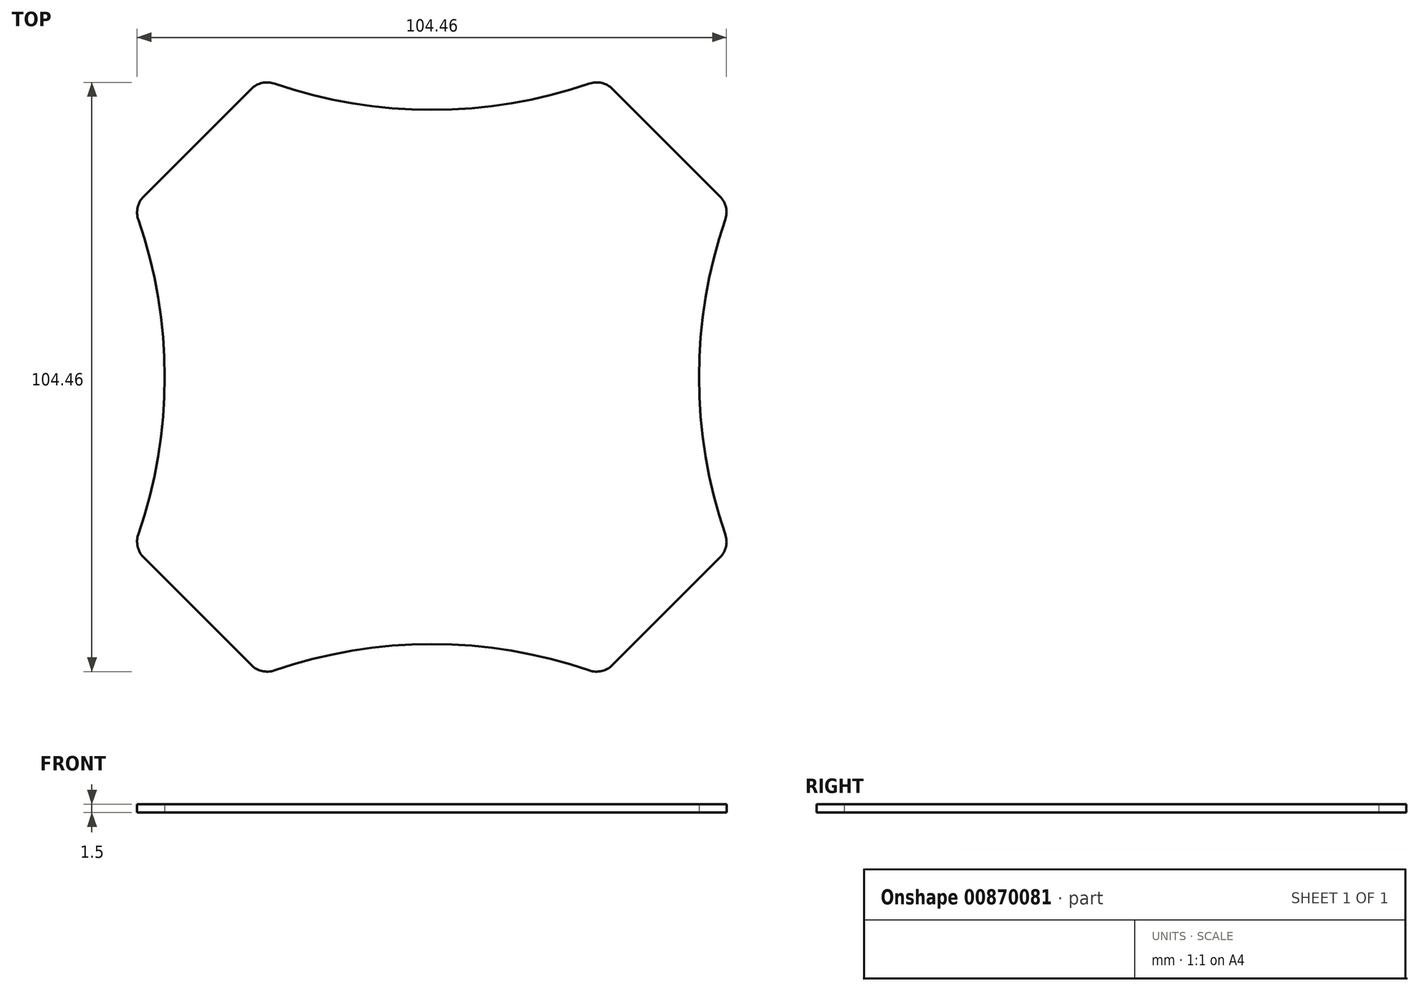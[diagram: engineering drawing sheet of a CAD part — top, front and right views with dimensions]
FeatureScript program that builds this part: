
annotation { "Feature Type Name" : "Feature", "Feature Type Description" : "" }
export const myFeature = defineFeature(function(context is Context, id is Id, definition is map)
    precondition{}
    {
        {
            var Q0;
            Q0=qCreatedBy(makeId("Top.planeOp"),FACE);
            var sketch = newSketch(context, id + "F0", { "sketchPlane" : qUnion([Q0])});
            skCircle(sketch, "E0.cCircle", {"center": v(0, 0) * mm, "radius": 58.75 * mm, "construction": true});
            skLineSegment(sketch, "E0.0", {"start": v(58.75, 24.34) * mm, "end": v(58.75, -24.34) * mm});
            skLineSegment(sketch, "E0.1", {"start": v(57.29, -25.8) * mm, "end": v(27.26, -55.82) * mm});
            skLineSegment(sketch, "E0.2", {"start": v(20.2, -58.75) * mm, "end": v(-20.2, -58.75) * mm});
            skLineSegment(sketch, "E0.3", {"start": v(-27.26, -55.82) * mm, "end": v(-57.29, -25.8) * mm});
            skLineSegment(sketch, "E0.4", {"start": v(-58.75, -24.34) * mm, "end": v(-58.75, 24.34) * mm});
            skLineSegment(sketch, "E0.5", {"start": v(-57.29, 25.8) * mm, "end": v(-27.26, 55.82) * mm});
            skLineSegment(sketch, "E0.6", {"start": v(-20.2, 58.75) * mm, "end": v(20.2, 58.75) * mm});
            skLineSegment(sketch, "E0.7", {"start": v(27.26, 55.82) * mm, "end": v(57.29, 25.8) * mm});
            skPoint(sketch, "E0.0.midPoint", {"position": v(58.75, 0) * mm});
            skLineSegment(sketch, "E1.bottom", {"start": v(60.82, 24.34) * mm, "end": v(85.75, 24.34) * mm});
            skLineSegment(sketch, "E1.top", {"start": v(60.82, -24.34) * mm, "end": v(85.75, -24.34) * mm});
            skLineSegment(sketch, "E1.right", {"start": v(90.75, 19.34) * mm, "end": v(90.75, -19.34) * mm});
            skLineSegment(sketch, "E2.bottom", {"start": v(-60.82, 24.34) * mm, "end": v(-85.75, 24.34) * mm});
            skLineSegment(sketch, "E2.top", {"start": v(-60.82, -24.34) * mm, "end": v(-85.75, -24.34) * mm});
            skLineSegment(sketch, "E2.left", {"start": v(-58.75, 24.34) * mm, "end": v(-58.75, -24.34) * mm});
            skLineSegment(sketch, "E2.right", {"start": v(-90.75, 19.34) * mm, "end": v(-90.75, -19.34) * mm});
            skPoint(sketch, "E3.visualSharp", {"position": v(-58.75, 24.34) * mm});
            skArc(sketch, "E3.filletArc", {"start": v(-60.82, 24.34) * mm, "mid": v(-58.9, 24.72) * mm, "end": v(-57.29, 25.8) * mm});
            skPoint(sketch, "E4.visualSharp", {"position": v(58.75, 24.34) * mm});
            skArc(sketch, "E4.filletArc", {"start": v(57.29, 25.8) * mm, "mid": v(58.9, 24.72) * mm, "end": v(60.82, 24.34) * mm});
            skPoint(sketch, "E5.visualSharp", {"position": v(24.34, 58.75) * mm});
            skArc(sketch, "E5.filletArc", {"start": v(27.26, 55.82) * mm, "mid": v(24.02, 57.99) * mm, "end": v(20.2, 58.75) * mm});
            skPoint(sketch, "E6.visualSharp", {"position": v(-24.34, 58.75) * mm});
            skArc(sketch, "E6.filletArc", {"start": v(-20.2, 58.75) * mm, "mid": v(-24.02, 57.99) * mm, "end": v(-27.26, 55.82) * mm});
            skPoint(sketch, "E7.visualSharp", {"position": v(24.34, -58.75) * mm});
            skArc(sketch, "E7.filletArc", {"start": v(20.2, -58.75) * mm, "mid": v(24.02, -57.99) * mm, "end": v(27.26, -55.82) * mm});
            skPoint(sketch, "E8.visualSharp", {"position": v(-24.34, -58.75) * mm});
            skArc(sketch, "E8.filletArc", {"start": v(-27.26, -55.82) * mm, "mid": v(-24.02, -57.99) * mm, "end": v(-20.2, -58.75) * mm});
            skPoint(sketch, "E9.visualSharp", {"position": v(-58.75, -24.34) * mm});
            skArc(sketch, "E9.filletArc", {"start": v(-57.29, -25.8) * mm, "mid": v(-58.9, -24.72) * mm, "end": v(-60.82, -24.34) * mm});
            skPoint(sketch, "E10.visualSharp", {"position": v(58.75, -24.34) * mm});
            skArc(sketch, "E10.filletArc", {"start": v(60.82, -24.34) * mm, "mid": v(58.9, -24.72) * mm, "end": v(57.29, -25.8) * mm});
            skPoint(sketch, "E11.visualSharp", {"position": v(90.75, -24.34) * mm});
            skArc(sketch, "E11.filletArc", {"start": v(85.75, -24.34) * mm, "mid": v(89.29, -22.87) * mm, "end": v(90.75, -19.34) * mm});
            skPoint(sketch, "E12.visualSharp", {"position": v(90.75, 24.34) * mm});
            skArc(sketch, "E12.filletArc", {"start": v(90.75, 19.34) * mm, "mid": v(89.29, 22.87) * mm, "end": v(85.75, 24.34) * mm});
            skPoint(sketch, "E13.visualSharp", {"position": v(-90.75, 24.34) * mm});
            skArc(sketch, "E13.filletArc", {"start": v(-85.75, 24.34) * mm, "mid": v(-89.29, 22.87) * mm, "end": v(-90.75, 19.34) * mm});
            skPoint(sketch, "E14.visualSharp", {"position": v(-90.75, -24.34) * mm});
            skArc(sketch, "E14.filletArc", {"start": v(-90.75, -19.34) * mm, "mid": v(-89.29, -22.87) * mm, "end": v(-85.75, -24.34) * mm});
            skLineSegment(sketch, "E15", {"start": v(-80.5, -24.34) * mm, "end": v(-80.5, -18.09) * mm});
            skLineSegment(sketch, "E16", {"start": v(-58.25, -18.09) * mm, "end": v(-84.25, -18.09) * mm});
            skLineSegment(sketch, "E17", {"start": v(-56.25, -16.09) * mm, "end": v(-56.25, -16.09) * mm});
            skLineSegment(sketch, "E18", {"start": v(-58.25, -14.09) * mm, "end": v(-84.25, -14.09) * mm});
            skLineSegment(sketch, "E19", {"start": v(-86.25, -16.09) * mm, "end": v(-86.25, -16.09) * mm});
            skLineSegment(sketch, "E20", {"start": v(-86.25, -14.09) * mm, "end": v(-90.75, -14.09) * mm});
            skLineSegment(sketch, "E21", {"start": v(-90.75, 0) * mm, "end": v(90.75, 0) * mm});
            skLineSegment(sketch, "E22", {"start": v(0, 58.75) * mm, "end": v(0, -58.75) * mm});
            skPoint(sketch, "E23.visualSharp", {"position": v(-86.25, -14.09) * mm});
            skArc(sketch, "E23.filletArc", {"start": v(-85.7, -14.09) * mm, "mid": v(-86.09, -14.25) * mm, "end": v(-86.25, -14.63) * mm});
            skArc(sketch, "E24.filletArc", {"start": v(-84.25, -14.09) * mm, "mid": v(-85.66, -14.67) * mm, "end": v(-86.25, -16.09) * mm});
            skPoint(sketch, "E25.visualSharp", {"position": v(-86.25, -18.09) * mm});
            skArc(sketch, "E25.filletArc", {"start": v(-86.25, -16.09) * mm, "mid": v(-85.66, -17.5) * mm, "end": v(-84.25, -18.09) * mm});
            skPoint(sketch, "E26.visualSharp", {"position": v(-56.25, -18.09) * mm});
            skArc(sketch, "E26.filletArc", {"start": v(-58.25, -18.09) * mm, "mid": v(-56.84, -17.5) * mm, "end": v(-56.25, -16.09) * mm});
            skPoint(sketch, "E27.visualSharp", {"position": v(-56.25, -14.09) * mm});
            skArc(sketch, "E27.filletArc", {"start": v(-56.25, -16.09) * mm, "mid": v(-56.84, -14.67) * mm, "end": v(-58.25, -14.09) * mm});
            skLineSegment(sketch, "E28.MirrorCS", {"start": v(-58.25, 14.09) * mm, "end": v(-84.25, 14.09) * mm});
            skArc(sketch, "E29.MirrorCS", {"start": v(-56.25, 16.09) * mm, "mid": v(-56.84, 14.67) * mm, "end": v(-58.25, 14.09) * mm});
            skArc(sketch, "E30.MirrorCS", {"start": v(-58.25, 18.09) * mm, "mid": v(-56.84, 17.5) * mm, "end": v(-56.25, 16.09) * mm});
            skLineSegment(sketch, "E31.MirrorCS", {"start": v(-58.25, 18.09) * mm, "end": v(-84.25, 18.09) * mm});
            skArc(sketch, "E32.MirrorCS", {"start": v(-86.25, 16.09) * mm, "mid": v(-85.66, 17.5) * mm, "end": v(-84.25, 18.09) * mm});
            skArc(sketch, "E33.MirrorCS", {"start": v(-84.25, 14.09) * mm, "mid": v(-85.66, 14.67) * mm, "end": v(-86.25, 16.09) * mm});
            skArc(sketch, "E34.MirrorCS", {"start": v(58.25, -18.09) * mm, "mid": v(56.84, -17.5) * mm, "end": v(56.25, -16.09) * mm});
            skArc(sketch, "E35.MirrorCS", {"start": v(56.25, -16.09) * mm, "mid": v(56.84, -14.67) * mm, "end": v(58.25, -14.09) * mm});
            skLineSegment(sketch, "E36.MirrorCS", {"start": v(58.25, -14.09) * mm, "end": v(84.25, -14.09) * mm});
            skArc(sketch, "E37.MirrorCS", {"start": v(84.25, -14.09) * mm, "mid": v(85.66, -14.67) * mm, "end": v(86.25, -16.09) * mm});
            skArc(sketch, "E38.MirrorCS", {"start": v(86.25, -16.09) * mm, "mid": v(85.66, -17.5) * mm, "end": v(84.25, -18.09) * mm});
            skLineSegment(sketch, "E39.MirrorCS", {"start": v(58.25, -18.09) * mm, "end": v(84.25, -18.09) * mm});
            skArc(sketch, "E40.MirrorCS", {"start": v(56.25, 16.09) * mm, "mid": v(56.84, 14.67) * mm, "end": v(58.25, 14.09) * mm});
            skArc(sketch, "E41.MirrorCS", {"start": v(58.25, 18.09) * mm, "mid": v(56.84, 17.5) * mm, "end": v(56.25, 16.09) * mm});
            skLineSegment(sketch, "E42.MirrorCS", {"start": v(58.25, 18.09) * mm, "end": v(84.25, 18.09) * mm});
            skArc(sketch, "E43.MirrorCS", {"start": v(86.25, 16.09) * mm, "mid": v(85.66, 17.5) * mm, "end": v(84.25, 18.09) * mm});
            skArc(sketch, "E44.MirrorCS", {"start": v(84.25, 14.09) * mm, "mid": v(85.66, 14.67) * mm, "end": v(86.25, 16.09) * mm});
            skLineSegment(sketch, "E45.MirrorCS", {"start": v(58.25, 14.09) * mm, "end": v(84.25, 14.09) * mm});
            skLineSegment(sketch, "E46.bottom", {"start": v(-41.75, -16) * mm, "end": v(-49.75, -16) * mm});
            skLineSegment(sketch, "E46.top", {"start": v(-41.75, 16) * mm, "end": v(-49.75, 16) * mm});
            skLineSegment(sketch, "E46.left", {"start": v(-39.75, -14) * mm, "end": v(-39.75, 14) * mm});
            skLineSegment(sketch, "E46.right", {"start": v(-51.75, -14) * mm, "end": v(-51.75, 14) * mm});
            skPoint(sketch, "E46.middle", {"position": v(-45.75, 0) * mm});
            skLineSegment(sketch, "E47", {"start": v(-51.75, 0) * mm, "end": v(-90.75, 0) * mm});
            skPoint(sketch, "E48.visualSharp", {"position": v(-51.75, 16) * mm});
            skArc(sketch, "E48.filletArc", {"start": v(-49.75, 16) * mm, "mid": v(-51.16, 15.41) * mm, "end": v(-51.75, 14) * mm});
            skPoint(sketch, "E49.visualSharp", {"position": v(-39.75, 16) * mm});
            skArc(sketch, "E49.filletArc", {"start": v(-39.75, 14) * mm, "mid": v(-40.34, 15.41) * mm, "end": v(-41.75, 16) * mm});
            skPoint(sketch, "E50.visualSharp", {"position": v(-39.75, -16) * mm});
            skArc(sketch, "E50.filletArc", {"start": v(-41.75, -16) * mm, "mid": v(-40.34, -15.41) * mm, "end": v(-39.75, -14) * mm});
            skPoint(sketch, "E51.visualSharp", {"position": v(-51.75, -16) * mm});
            skArc(sketch, "E51.filletArc", {"start": v(-51.75, -14) * mm, "mid": v(-51.16, -15.41) * mm, "end": v(-49.75, -16) * mm});
            skLineSegment(sketch, "E52.MirrorCS", {"start": v(39.75, -14) * mm, "end": v(39.75, 14) * mm});
            skArc(sketch, "E53.MirrorCS", {"start": v(39.75, 14) * mm, "mid": v(40.34, 15.41) * mm, "end": v(41.75, 16) * mm});
            skLineSegment(sketch, "E54.MirrorCS", {"start": v(41.75, 16) * mm, "end": v(49.75, 16) * mm});
            skArc(sketch, "E55.MirrorCS", {"start": v(49.75, 16) * mm, "mid": v(51.16, 15.41) * mm, "end": v(51.75, 14) * mm});
            skLineSegment(sketch, "E56.MirrorCS", {"start": v(51.75, -14) * mm, "end": v(51.75, 14) * mm});
            skArc(sketch, "E57.MirrorCS", {"start": v(51.75, -14) * mm, "mid": v(51.16, -15.41) * mm, "end": v(49.75, -16) * mm});
            skLineSegment(sketch, "E58.MirrorCS", {"start": v(41.75, -16) * mm, "end": v(49.75, -16) * mm});
            skArc(sketch, "E59.MirrorCS", {"start": v(41.75, -16) * mm, "mid": v(40.34, -15.41) * mm, "end": v(39.75, -14) * mm});
            skCircle(sketch, "E60", {"center": v(0, 0) * mm, "radius": 7.5 * mm});
            skSolve(sketch);
        }
        {
            var Q0;
            Q0=qCreatedBy(makeId("Top.planeOp"),FACE);
            var sketch = newSketch(context, id + "F1", { "sketchPlane" : qUnion([Q0])});
            skPoint(sketch, "E61.0.midPoint", {"position": v(0, 58.75) * mm});
            skLineSegment(sketch, "E62", {"start": v(-41.54, 41.54) * mm, "end": v(-30.23, 52.86) * mm});
            skLineSegment(sketch, "E63", {"start": v(-41.54, 41.54) * mm, "end": v(-52.86, 30.23) * mm});
            skPoint(sketch, "E64.center", {"position": v(0, 0) * mm});
            skLineSegment(sketch, "E65", {"start": v(0, 52.86) * mm, "end": v(0, 47.36) * mm, "construction": true});
            skArc(sketch, "E66.1.0", {"start": v(-52.86, -30.23) * mm, "mid": v(-47.36, 0) * mm, "end": v(-52.86, 30.23) * mm});
            skArc(sketch, "E67.1.0", {"start": v(30.23, -52.86) * mm, "mid": v(0, -47.36) * mm, "end": v(-30.23, -52.86) * mm});
            skArc(sketch, "E67.2.0", {"start": v(52.86, 30.23) * mm, "mid": v(47.36, 0) * mm, "end": v(52.86, -30.23) * mm});
            skArc(sketch, "E67.3.0", {"start": v(-30.23, 52.86) * mm, "mid": v(0, 47.36) * mm, "end": v(30.23, 52.86) * mm});
            skLineSegment(sketch, "E68.1.0", {"start": v(-41.54, -41.54) * mm, "end": v(-52.86, -30.23) * mm});
            skLineSegment(sketch, "E68.1.1", {"start": v(-41.54, -41.54) * mm, "end": v(-30.23, -52.86) * mm});
            skLineSegment(sketch, "E68.2.0", {"start": v(41.54, -41.54) * mm, "end": v(30.23, -52.86) * mm});
            skLineSegment(sketch, "E68.2.1", {"start": v(41.54, -41.54) * mm, "end": v(52.86, -30.23) * mm});
            skLineSegment(sketch, "E68.3.0", {"start": v(41.54, 41.54) * mm, "end": v(52.86, 30.23) * mm});
            skLineSegment(sketch, "E68.3.1", {"start": v(41.54, 41.54) * mm, "end": v(30.23, 52.86) * mm});
            skSolve(sketch);
        }
        {
            var Q0;
            Q0 = qSketchRegion(id + "F1", true);
            extrude(context, id + "F2", {"entities" : qUnion([Q0]), "depth" : 1.5 * mm, "offsetDistance" : 25 * mm});
        }
        {
            var Q0;
            Q0=makeQuery(id+"F2.opExtrude","SWEPT_EDGE",EDGE,{"disambiguationData":[OSD([sQuery(id+"F1.wireOp",EDGE,"E63"),sQuery(id+"F1.wireOp",EDGE,"E66.1.0")])]});
            var Q1;
            Q1=makeQuery(id+"F2.opExtrude","SWEPT_EDGE",EDGE,{"disambiguationData":[OSD([sQuery(id+"F1.wireOp",EDGE,"E62"),sQuery(id+"F1.wireOp",EDGE,"E67.3.0")])]});
            var Q2;
            Q2=makeQuery(id+"F2.opExtrude","SWEPT_EDGE",EDGE,{"disambiguationData":[OSD([sQuery(id+"F1.wireOp",EDGE,"E67.3.0"),sQuery(id+"F1.wireOp",EDGE,"E68.3.1")])]});
            var Q3;
            Q3=makeQuery(id+"F2.opExtrude","SWEPT_EDGE",EDGE,{"disambiguationData":[OSD([sQuery(id+"F1.wireOp",EDGE,"E67.2.0"),sQuery(id+"F1.wireOp",EDGE,"E68.3.0")])]});
            var Q4;
            Q4=makeQuery(id+"F2.opExtrude","SWEPT_EDGE",EDGE,{"disambiguationData":[OSD([sQuery(id+"F1.wireOp",EDGE,"E67.2.0"),sQuery(id+"F1.wireOp",EDGE,"E68.2.1")])]});
            var Q5;
            Q5=makeQuery(id+"F2.opExtrude","SWEPT_EDGE",EDGE,{"disambiguationData":[OSD([sQuery(id+"F1.wireOp",EDGE,"E67.1.0"),sQuery(id+"F1.wireOp",EDGE,"E68.2.0")])]});
            var Q6;
            Q6=makeQuery(id+"F2.opExtrude","SWEPT_EDGE",EDGE,{"disambiguationData":[OSD([sQuery(id+"F1.wireOp",EDGE,"E67.1.0"),sQuery(id+"F1.wireOp",EDGE,"E68.1.1")])]});
            var Q7;
            Q7=makeQuery(id+"F2.opExtrude","SWEPT_EDGE",EDGE,{"disambiguationData":[OSD([sQuery(id+"F1.wireOp",EDGE,"E66.1.0"),sQuery(id+"F1.wireOp",EDGE,"E68.1.0")])]});
            fillet(context, id + "F3", {"entities" : qUnion([Q0, Q1, Q2, Q3, Q4, Q5, Q6, Q7]), "radius" : 4 * mm, "tangentPropagation" : true, "allowEdgeOverflow" : false});
        }
    });
